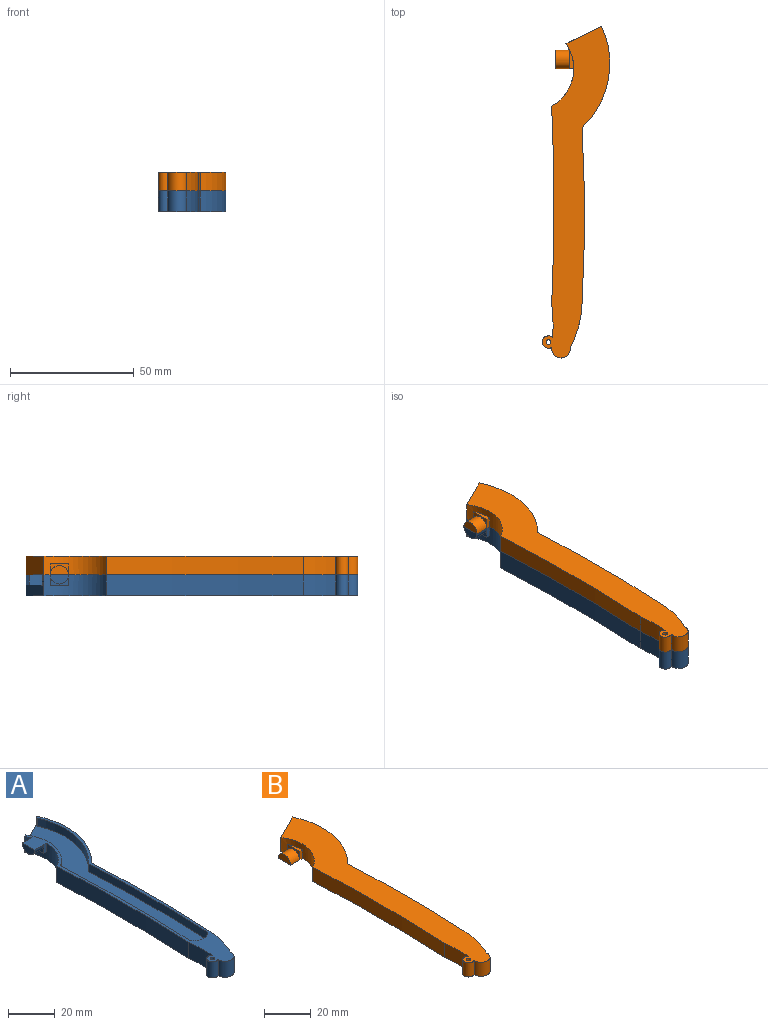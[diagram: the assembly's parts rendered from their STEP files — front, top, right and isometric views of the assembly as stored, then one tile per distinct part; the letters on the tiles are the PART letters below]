
ASSEMBLY  parts=2 mates=1
PART A: 24 faces, bbox 27.3x134.2x8.4 mm
  f0: plane 4.4x1.71mm, normal (0,-1,0), area 7.5mm2, adj f2,f9,f19,f23
  f1: plane 7.5x3.75mm, normal (-1,0,0), area 22.1mm2, adj f2,f22
  f2: plane 134.18x27.3mm, normal (0,0,1), area 549mm2, adj f0,f1,f4,f6,f7,f8,f9,f10
  f3: plane 134.18x27.3mm, normal (0,0,-1), area 1676.7mm2, adj f9,f10,f11,f12,f13,f14,f15,f16
  f4: cylinder r=18.63mm len=26.49mm, axis (0,0,-1), area 127.3mm2, adj f2,f5,f8,f20
  f5: plane 114.49x20.88mm, normal (0,0,1), area 1178.3mm2, adj f4,f6,f7,f8,f17,f20,f21
  f6: cylinder r=640mm len=71.8mm, axis (0,0,-1), area 301.7mm2, adj f2,f5,f7,f17
  f7: cylinder r=6mm len=9.62mm, axis (0,0,-1), area 47.1mm2, adj f2,f5,f6,f8
  f8: cylinder r=770mm len=78.6mm, axis (0,0,-1), area 330.3mm2, adj f2,f4,f5,f7
  f9: cylinder r=17.33mm len=25.17mm, axis (0,0,-1), area 210.7mm2, adj f0,f2,f3,f10,f19,f20,f23
  f10: cylinder r=768.7mm len=79.73mm, axis (0,0,-1), area 670mm2, adj f2,f3,f9,f11
  f11: cylinder r=70mm len=13.82mm, axis (0,0,-1), area 116.3mm2, adj f2,f3,f10,f12
  f12: cylinder r=2.5mm len=8.4mm, axis (0,0,-1), area 93mm2, adj f2,f3,f11,f13
  f13: cylinder r=3.8mm len=8.4mm, axis (0,0,-1), area 108.4mm2, adj f2,f3,f12,f14
  f14: cylinder r=40mm len=17.8mm, axis (0,0,-1), area 156.1mm2, adj f2,f3,f13,f15
  f15: cylinder r=641.3mm len=70.96mm, axis (0,0,-1), area 596.4mm2, adj f2,f3,f14,f16
  f16: cylinder r=35.8mm len=41.14mm, axis (0,0,-1), area 375.8mm2, adj f2,f3,f15,f20,f21
  f17: cylinder r=34.5mm len=39.3mm, axis (0,0,-1), area 180.1mm2, adj f2,f5,f6,f21
  f18: cylinder r=1mm len=8.4mm, axis (0,0,-1), area 52.8mm2, adj f2,f3
  f19: plane 7.5x1.71mm, normal (0,0,-1), area 8.6mm2, adj f0,f9,f23
  f20: plane 14.4x8.4mm, normal (-0.45,0.89,0), area 73.1mm2, adj f2,f3,f4,f5,f9,f16
  f21: plane 4.2x1.3mm, normal (-0.84,0.54,0), area 6.5mm2, adj f2,f5,f16,f17
  f22: cylinder r=3.75mm len=7.5mm, axis (-1,0,0), area 65.9mm2, adj f1,f2,f23
  f23: plane 7.51x4.41mm, normal (-1,0,0), area 10.9mm2, adj f0,f9,f19,f22
PART B: 17 faces, bbox 27.3x134.2x7.4 mm
  f0: plane 4.4x1.71mm, normal (0,-1,0), area 7.5mm2, adj f3,f11,f13,f15
  f1: cylinder r=35.8mm len=41.14mm, axis (0,0,1), area 331.1mm2, adj f2,f9,f11,f16
  f2: plane 14.4x7.4mm, normal (-0.45,0.89,0), area 119.1mm2, adj f1,f3,f11,f16
  f3: cylinder r=17.33mm len=25.17mm, axis (0,0,1), area 181.5mm2, adj f0,f2,f4,f11,f13,f15,f16
  f4: cylinder r=768.7mm len=79.73mm, axis (0,0,1), area 590.2mm2, adj f3,f5,f11,f16
  f5: cylinder r=70mm len=13.82mm, axis (0,0,1), area 102.5mm2, adj f4,f6,f11,f16
  f6: cylinder r=2.5mm len=7.4mm, axis (0,0,1), area 81.9mm2, adj f5,f7,f11,f16
  f7: cylinder r=3.8mm len=7.6mm, axis (0,0,1), area 95.5mm2, adj f6,f8,f11,f16
  f8: cylinder r=40mm len=17.8mm, axis (0,0,1), area 137.5mm2, adj f7,f9,f11,f16
  f9: cylinder r=641.3mm len=70.96mm, axis (0,0,1), area 525.4mm2, adj f1,f8,f11,f16
  f10: cylinder r=1mm len=7.4mm, axis (0,0,1), area 46.5mm2, adj f11,f16
  f11: plane 134.18x27.3mm, normal (0,0,-1), area 1727.3mm2, adj f0,f1,f2,f3,f4,f5,f6,f7
  f12: plane 7.5x3.75mm, normal (-1,0,0), area 22.1mm2, adj f11,f14
  f13: plane 7.5x1.71mm, normal (0,0,1), area 8.6mm2, adj f0,f3,f15
  f14: cylinder r=3.75mm len=7.5mm, axis (-1,0,0), area 65.9mm2, adj f11,f12,f15
  f15: plane 7.51x4.41mm, normal (-1,0,0), area 10.9mm2, adj f0,f3,f13,f14
  f16: plane 134.18x27.3mm, normal (0,0,1), area 1676.7mm2, adj f1,f2,f3,f4,f5,f6,f7,f8
PLACE A t=(35.78,51.73,33.43)mm
PLACE B t=(36.62,53.03,50.23)mm
MATE fastened A.f2 <-> B.f11  axis (0,0,1) through (18.1,39.58,41.83)mm
